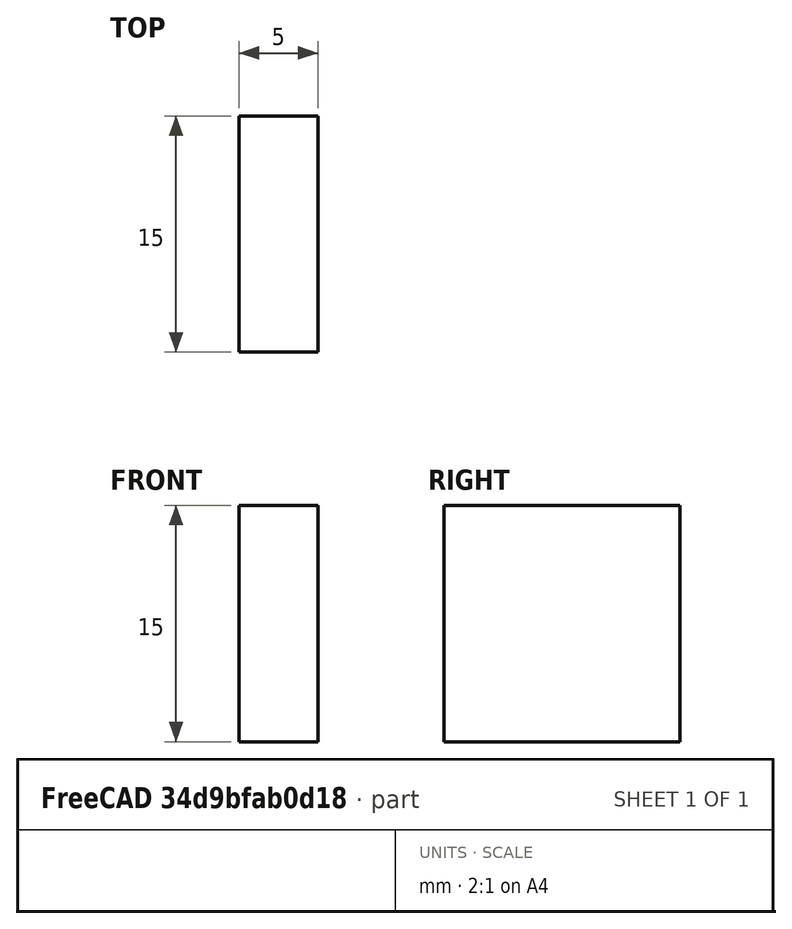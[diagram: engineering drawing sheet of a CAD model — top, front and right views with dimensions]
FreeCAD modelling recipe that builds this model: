
FCSTD DOCUMENT  (FreeCAD 0.20R29177 (Git))
Label: clap
License: All rights reserved
LicenseURL: http://en.wikipedia.org/wiki/All_rights_reserved
objects: Sketcher::SketchObject×1, Spreadsheet::Sheet×1, PartDesign::Pad×1, PartDesign::Body×1, App::Part×1
note: 4 computed .brp shape members not serialized (recipe doc carries the construction recipe); baked Part::Feature solids carry a one-line shape summary decoded from their .brp

FEATURE [Sketcher::SketchObject] Sketch
  FullyConstrained = true
  MapMode = 5
  Support = -> [XY_Plane001]
  expr: Constraints[10] = Spreadsheet.thickness
  expr: Constraints[11] = Spreadsheet.width / 2
  expr: Constraints[9] = Spreadsheet.width
  sketch-geometry (4):
    g0: LineSegment StartX=0 StartY=7.5 StartZ=0 EndX=5 EndY=7.5 EndZ=0
    g1: LineSegment StartX=5 StartY=7.5 StartZ=0 EndX=5 EndY=-7.5 EndZ=0
    g2: LineSegment StartX=5 StartY=-7.5 StartZ=0 EndX=0 EndY=-7.5 EndZ=0
    g3: LineSegment StartX=0 StartY=-7.5 StartZ=0 EndX=0 EndY=7.5 EndZ=0
  constraints (12):
    c: Coincident(g0,g1)
    c: Coincident(g1,g2)
    c: Coincident(g2,g3)
    c: Coincident(g3,g0)
    c: Horizontal(g0)
    c: Horizontal(g2)
    c: Vertical(g1)
    c: Vertical(g3)
    c: PointOnObject(g0,g-2)
    c: DistanceY(g1,g1) = 15
    c: DistanceX(g0,g0) = 5
    c: DistanceY(g0) = 7.5
FEATURE [Spreadsheet::Sheet] Spreadsheet
  cells = A2=width; B2(width)=15; A3=height; B3(height)=15; A4=gap; B4(gap)=2.3622; A5=thickness; B5(thickness)=5
FEATURE [PartDesign::Pad] Pad
  Direction = (0,0,1)
  Length = 15
  Length2 = 10
  Profile = -> Sketch
  ReferenceAxis = -> Sketch [N_Axis]
  Type = 0
  expr: Length = Spreadsheet.height
FEATURE [PartDesign::Body] Body
  Group = -> [Sketch,Pad]
  Origin = -> Origin001
  Tip = -> Pad
FEATURE [App::Part] Part
  Group = -> [Body]
  Origin = -> Origin
